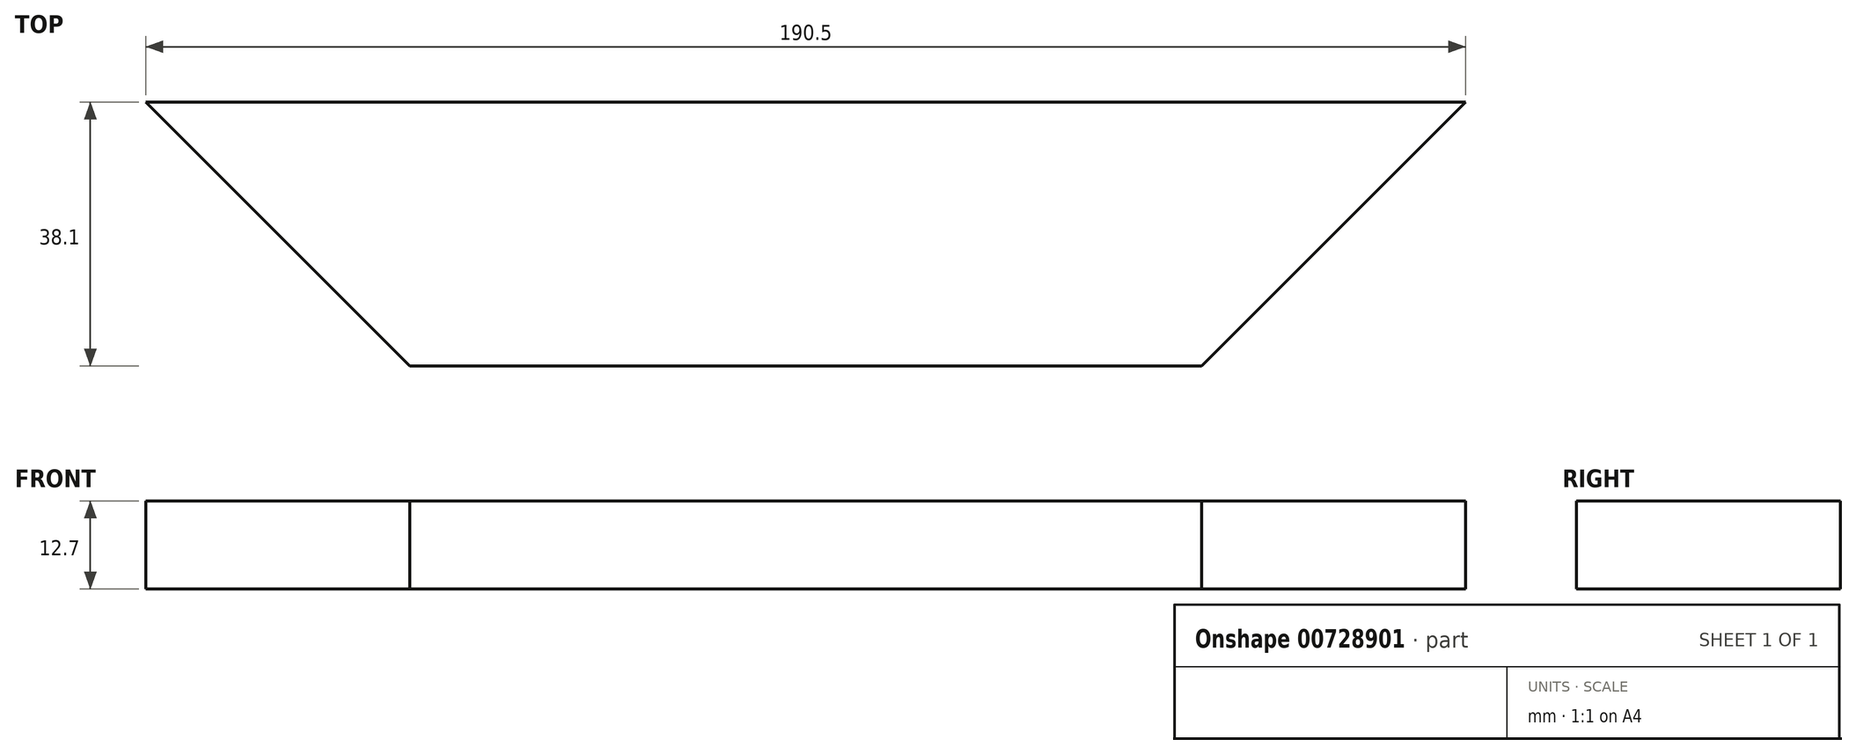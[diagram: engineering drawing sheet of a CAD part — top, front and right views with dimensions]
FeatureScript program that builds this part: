
annotation { "Feature Type Name" : "Feature", "Feature Type Description" : "" }
export const myFeature = defineFeature(function(context is Context, id is Id, definition is map)
    precondition{}
    {
        {
            var Q0;
            Q0=qCreatedBy(makeId("Top.planeOp"),FACE);
            var sketch = newSketch(context, id + "F0", { "sketchPlane" : qUnion([Q0])});
            skLineSegment(sketch, "E0.bottom", {"start": v(95.25, 19.05) * mm, "end": v(-95.25, 19.05) * mm});
            skLineSegment(sketch, "E0.top", {"start": v(95.25, -19.05) * mm, "end": v(-95.25, -19.05) * mm});
            skLineSegment(sketch, "E0.left", {"start": v(95.25, 19.05) * mm, "end": v(95.25, -19.05) * mm});
            skLineSegment(sketch, "E0.right", {"start": v(-95.25, 19.05) * mm, "end": v(-95.25, -19.05) * mm});
            skPoint(sketch, "E0.middle", {"position": v(0, 0) * mm});
            skLineSegment(sketch, "E1", {"start": v(-95.25, 19.05) * mm, "end": v(-57.15, -19.05) * mm});
            skLineSegment(sketch, "E2", {"start": v(95.25, 19.05) * mm, "end": v(57.15, -19.05) * mm});
            skSolve(sketch);
        }
        {
            var Q0;
            Q0=makeQuery(id+"F0.imprint","IMPRINT",FACE,{"disambiguationData":[TD([[makeQuery(id+"F0.imprint","IMPRINT",EDGE,{"derivedFrom":sQuery(id+"F0.wireOp",EDGE,"E0.bottom")}),1.0]])]});
            extrude(context, id + "F1", {"entities" : qUnion([Q0]), "oppositeDirection" : true, "depth" : 12.7 * mm, "offsetDistance" : 25.4 * mm});
        }
    });
